# Revit family: Camera-Security-Panasonic-Network-S6130Y
name_source: partatom
category: Security Devices
revit_build: Autodesk Revit 2016 (Build: 20150714_1515(x64)
units: mm (PartAtom-declared; Revit-internal decimal feet)

## family parameters
Cut with Voids When Loaded = No
Host = Face
Maintain Annotation Orientation = No
OmniClass Number = 23.85.10.14.11
OmniClass Title = Cameras
Part Type = Normal
Room Calculation Point = No
Round Connector Dimension = Use Diameter
Shared = No

## types (1)
- Standard, WV-S6130
    Alarm Input Or Output Specification = ALARM IN 1 (Black & white input, Auto time adjustment input) (x1), ALARM IN 2 (ALARM OUT) (x1), ALARM IN 3 (AUX OUT) (x1)
    Angle Of View = 74
    Audio In = Yes
    Audio Out = Yes
    Communication Ports = 10Base-T / 100Base-TX, RJ-45
    Date Last Modified = August, 1, 2017
    Day Or Night = Yes
    Default Elevation = 48 "
    Description = "Security Camera, H.264/H.265, Full HD, 21x Optical Zoom, Indoor, PTZ, Network, WV-S6130"
    Diameter = 4.528 "
    Equipment Abbreviation = SC
    Family Version = 1.0.0
    HFOV Max 169 = 74.00°
    HFOV Max 43 = 61.00°
    HFOV Min 169 = 3.50°
    HFOV Min 43 = 3.00°
    Has POE = Yes
    Height = 6.102 "
    IP Or Analog = IP
    Indoor Or Outdoor = Indoor
    Manufacturer = Panasonic
    Minimum Illumination = 0.015 lx
    Model = "WV-S6130"
    Model Disclaimer = Contact Panasonic for more information
    Mounting Positions = Mount Dependent or Surface Mount
    Operational Humidity = 10 to 90 % (no condensation)
    Operational Temperature = 14°F - 122°F
    Pan Max = 350.00°
    Pan Min = 0.00°
    Panning Range = 0 to +350
    Part Description = "Security Camera, H.264/H.265, Full HD, 21x Optical Zoom, Indoor, PTZ, Network, WV-S6130"
    Part Number = "WV-S6130"
    Power Active = 12.0 W
    Product Documentation Link = http://ssbu-t.psn-web.net
    Product Material = Paint - Panasonic - Silver
    Product Page URL = https://security.panasonic.com
    Provide Feedback = https://www.surveymonkey.com
    Regulatory Compliance = UL60950-1, C-UL CAN/CSA C22.2 No.60950-1, CE, IEC60950-1, FCC Part15 Class A, ICES-003 Class A, EN55022 Class B, EN55024
    Storage Temperature = 14 °F to 122 °F
    Tilt Max = 90.00°
    Tilt Min = -30.00°
    Tilting Range = -30 to +90
    URL = http://security.panasonic.com
    VFOV Max 169 = 42.00°
    VFOV Max 43 = 46.00°
    VFOV Min 169 = 2.00°
    VFOV Min 43 = 2.30°
    Vandal Resistant = No
    Voltage DC = 12.00 V
    Weight = 2.43 lb
    Wide Dynamic Range = Yes
    z Base Diameter = 7.283 "
    z Bottom of Dome Diameter = 4.528 "
    z Bottom of Dome Distance = 1.496 "
    z Camera Resolution Type = 0
    z Const Pan Handle Length = 27.559 "
    z Const Tilt Base Length = 9.843 "
    z Const Tilt Base2 Length = 19.685 "
    z Const Tilt Handle Length = 14.173 "
    z Const Yaw Base Length = 10.236 "
    z Const Yaw Base2 Length = 17.323 "
    z Const Yaw Handle Length = 9.252 "
    z Dome Diameter = 4.528 "
    z VV Viewpoint Depth Max = 1.685 "
    z VV Viewpoint Depth Min = 1.685 "

## geometry (parser evidence)
native form markers: Blend x2, Sweep x6
no freeform markers — native parametric forms only
